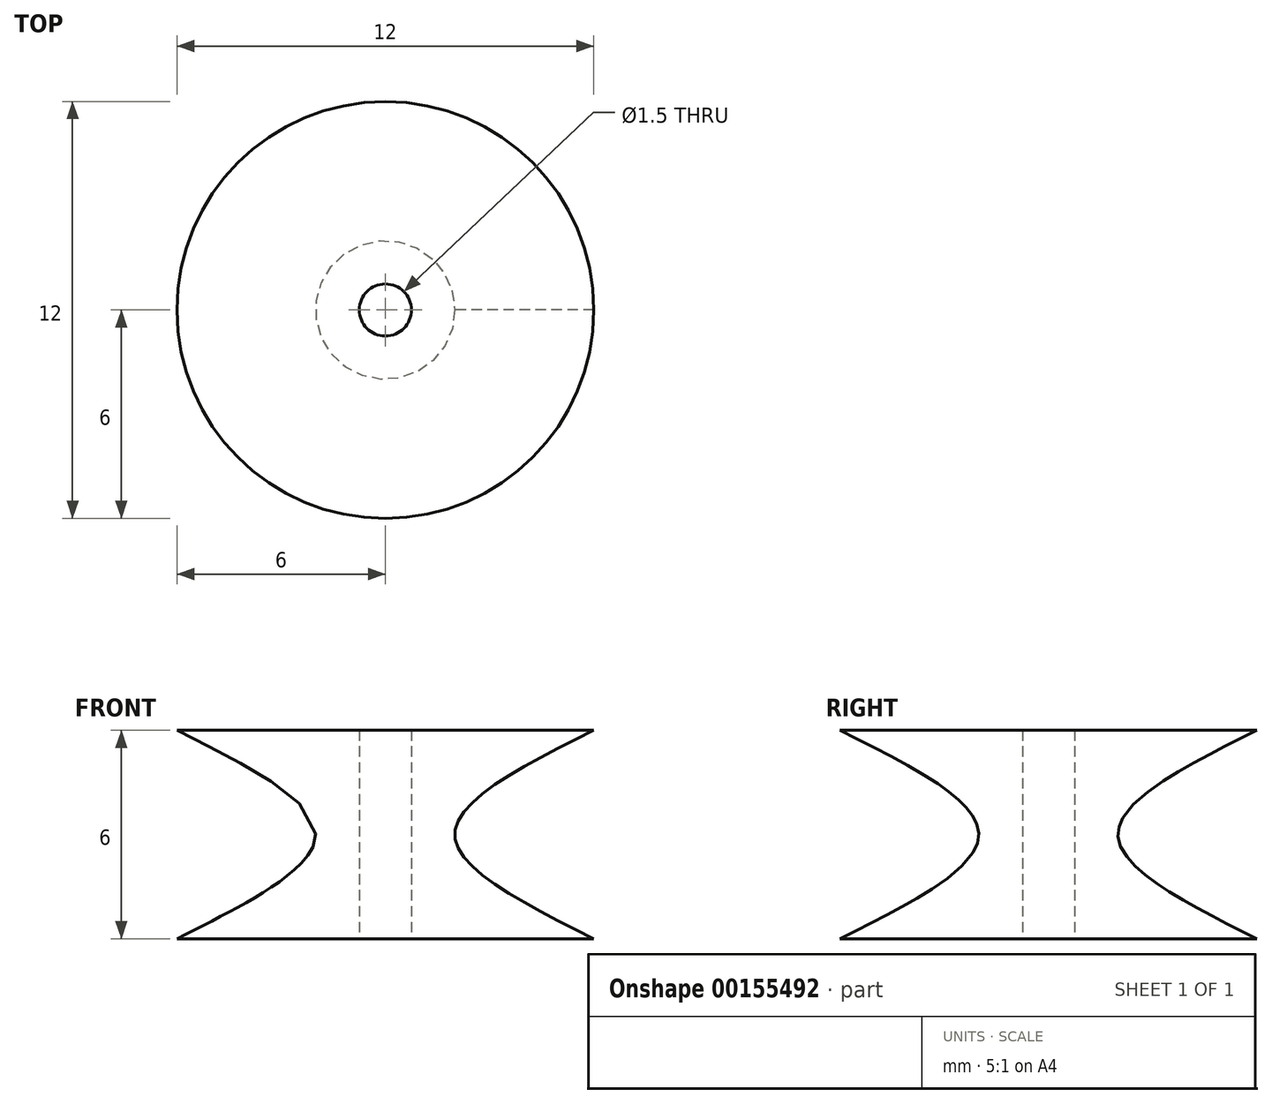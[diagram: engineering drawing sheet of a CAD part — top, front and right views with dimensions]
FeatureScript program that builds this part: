
annotation { "Feature Type Name" : "Feature", "Feature Type Description" : "" }
export const myFeature = defineFeature(function(context is Context, id is Id, definition is map)
    precondition{}
    {
        {
            var Q0;
            Q0=qCreatedBy(makeId("Top.planeOp"),FACE);
            var sketch = newSketch(context, id + "F0", { "sketchPlane" : qUnion([Q0])});
            skCircle(sketch, "E0", {"center": v(0, 0) * mm, "radius": 6 * mm});
            skPoint(sketch, "E1", {"position": v(0, 6) * mm});
            skPoint(sketch, "E2", {"position": v(0, -6) * mm});
            skPoint(sketch, "E3", {"position": v(-6, 0) * mm});
            skPoint(sketch, "E4", {"position": v(6, 0) * mm});
            skSolve(sketch);
        }
        {
            var Q0;
            Q0=qCreatedBy(makeId("Top.planeOp"),FACE);
            cPlane(context, id + "F1", {"entities" : qUnion([Q0]), "cplaneType" : CPlaneType.OFFSET, "offset" : 3 * mm, "width" : 150 * mm, "height" : 150 * mm});
        }
        {
            var Q0;
            Q0=qCreatedBy(id+"F1.planeOp",FACE);
            var sketch = newSketch(context, id + "F2", { "sketchPlane" : qUnion([Q0])});
            skCircle(sketch, "E5", {"center": v(0, 0) * mm, "radius": 2 * mm});
            skPoint(sketch, "E6", {"position": v(0, 2) * mm});
            skPoint(sketch, "E7", {"position": v(-2, 0) * mm});
            skPoint(sketch, "E8", {"position": v(0, -2) * mm});
            skPoint(sketch, "E9", {"position": v(2, 0) * mm});
            skSolve(sketch);
        }
        {
            var Q0;
            Q0=qCreatedBy(makeId("Top.planeOp"),FACE);
            cPlane(context, id + "F3", {"entities" : qUnion([Q0]), "cplaneType" : CPlaneType.OFFSET, "offset" : 6 * mm, "width" : 150 * mm, "height" : 150 * mm});
        }
        {
            var Q0;
            Q0=qCreatedBy(id+"F3.planeOp",FACE);
            var sketch = newSketch(context, id + "F4", { "sketchPlane" : qUnion([Q0])});
            skCircle(sketch, "E10", {"center": v(0, 0) * mm, "radius": 6 * mm});
            skPoint(sketch, "E11", {"position": v(0, 6) * mm});
            skPoint(sketch, "E12", {"position": v(-6, 0) * mm});
            skPoint(sketch, "E13", {"position": v(0, -6) * mm});
            skPoint(sketch, "E14", {"position": v(6, 0) * mm});
            skSolve(sketch);
        }
        {
            var Q0;
            Q0=makeQuery(id+"F0.imprint","IMPRINT",FACE,{"disambiguationData":[TD([[makeQuery(id+"F0.imprint","IMPRINT",EDGE,{"derivedFrom":sQuery(id+"F0.wireOp",EDGE,"E0")}),1.0]])]});
            var Q1;
            Q1=makeQuery(id+"F2.imprint","IMPRINT",FACE,{"disambiguationData":[TD([[makeQuery(id+"F2.imprint","IMPRINT",EDGE,{"derivedFrom":sQuery(id+"F2.wireOp",EDGE,"E5")}),1.0]])]});
            var Q2;
            Q2=makeQuery(id+"F4.imprint","IMPRINT",FACE,{"disambiguationData":[TD([[makeQuery(id+"F4.imprint","IMPRINT",EDGE,{"derivedFrom":sQuery(id+"F4.wireOp",EDGE,"E10")}),1.0]])]});
            loft(context, id + "F5", {"sheetProfilesArray" : [{ "sheetProfileEntities" : qUnion([Q0]) }, { "sheetProfileEntities" : qUnion([Q1]) }, { "sheetProfileEntities" : qUnion([Q2]) }]});
        }
        {
            var Q0;
            Q0=sQuery(id+"F0.wireOp",VERTEX,"E0.center");
            var Q1;
            Q1=makeQuery(id+"F5.opLoft","SWEPT_BODY",BODY,{"disambiguationData":[OSD([makeQuery(id+"F0.imprint","IMPRINT",FACE,{"disambiguationData":[TD([[makeQuery(id+"F0.imprint","IMPRINT",EDGE,{"derivedFrom":sQuery(id+"F0.wireOp",EDGE,"E0")}),1.0]])]}),sQuery(id+"F2.wireOp",EDGE,"E5"),makeQuery(id+"F4.imprint","IMPRINT",FACE,{"disambiguationData":[TD([[makeQuery(id+"F4.imprint","IMPRINT",EDGE,{"derivedFrom":sQuery(id+"F4.wireOp",EDGE,"E10")}),1.0]])]})])]});
            hole(context, id + "F6", {"style" : HoleStyle.SIMPLE, "endStyle" : HoleEndStyle.THROUGH, "oppositeDirection" : true, "holeDiameter" : 1.5 * mm, "locations" : qUnion([Q0]), "scope" : qUnion([Q1]), "isTappedThrough" : true});
        }
    });
